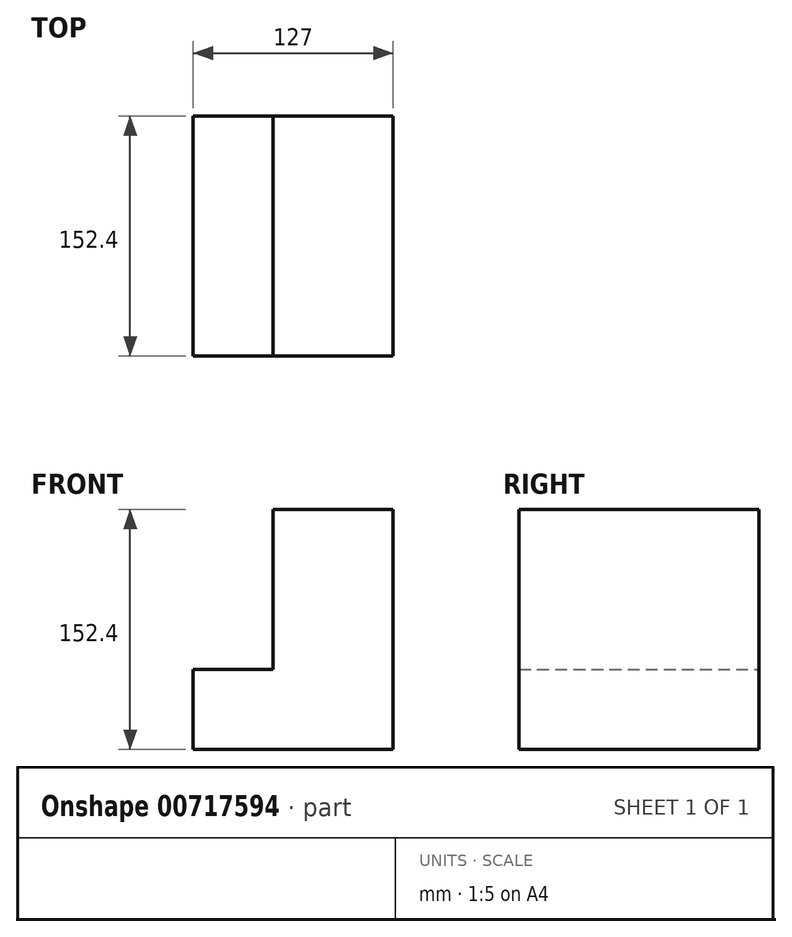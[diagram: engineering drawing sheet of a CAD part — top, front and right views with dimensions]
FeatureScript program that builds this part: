
annotation { "Feature Type Name" : "Feature", "Feature Type Description" : "" }
export const myFeature = defineFeature(function(context is Context, id is Id, definition is map)
    precondition{}
    {
        {
            var Q0;
            Q0=qCreatedBy(makeId("Front.planeOp"),FACE);
            var sketch = newSketch(context, id + "F0", { "sketchPlane" : qUnion([Q0])});
            skLineSegment(sketch, "E0", {"start": v(-97.33, -39.87) * mm, "end": v(-97.33, 10.93) * mm});
            skLineSegment(sketch, "E1", {"start": v(-97.33, 10.93) * mm, "end": v(-46.53, 10.93) * mm});
            skLineSegment(sketch, "E2", {"start": v(-46.53, 10.93) * mm, "end": v(-46.53, 112.53) * mm});
            skLineSegment(sketch, "E3", {"start": v(-46.53, 112.53) * mm, "end": v(29.67, 112.53) * mm});
            skLineSegment(sketch, "E4", {"start": v(29.67, 112.53) * mm, "end": v(29.67, -39.87) * mm});
            skLineSegment(sketch, "E5", {"start": v(29.67, -39.87) * mm, "end": v(-97.33, -39.87) * mm});
            skSolve(sketch);
        }
        {
            var Q0;
            Q0=makeQuery(id+"F0.imprint","IMPRINT",FACE,{"disambiguationData":[TD([[makeQuery(id+"F0.imprint","IMPRINT",EDGE,{"derivedFrom":sQuery(id+"F0.wireOp",EDGE,"E0")}),-1.0]])]});
            extrude(context, id + "F1", {"entities" : qUnion([Q0]), "depth" : 152.4 * mm, "offsetDistance" : 25.4 * mm});
        }
    });
